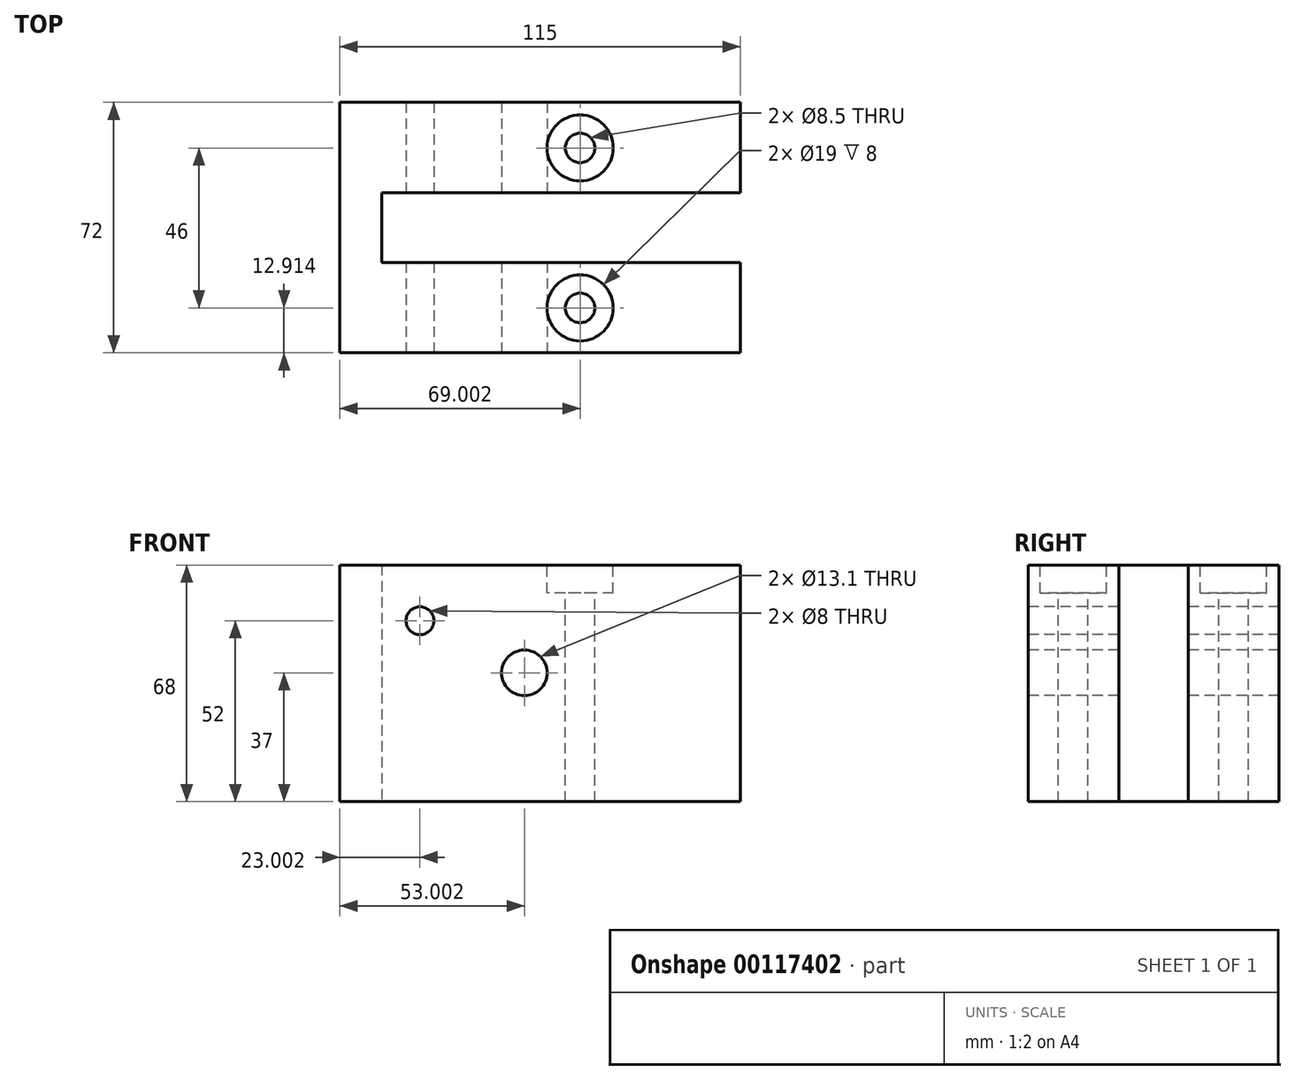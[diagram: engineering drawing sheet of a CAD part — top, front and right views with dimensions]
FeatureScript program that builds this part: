
annotation { "Feature Type Name" : "Feature", "Feature Type Description" : "" }
export const myFeature = defineFeature(function(context is Context, id is Id, definition is map)
    precondition{}
    {
        {
            var Q0;
            Q0=qCreatedBy(makeId("Top.planeOp"),FACE);
            var sketch = newSketch(context, id + "F0", { "sketchPlane" : qUnion([Q0])});
            skLineSegment(sketch, "E0.bottom", {"start": v(66.85, 38.03) * mm, "end": v(-48.15, 38.03) * mm});
            skLineSegment(sketch, "E0.top", {"start": v(66.85, -33.97) * mm, "end": v(-48.15, -33.97) * mm});
            skLineSegment(sketch, "E0.right", {"start": v(-48.15, 38.03) * mm, "end": v(-48.15, -33.97) * mm});
            skLineSegment(sketch, "E1.bottom", {"start": v(66.85, 12.03) * mm, "end": v(-36.15, 12.03) * mm});
            skLineSegment(sketch, "E1.top", {"start": v(66.85, -7.97) * mm, "end": v(-36.15, -7.97) * mm});
            skLineSegment(sketch, "E1.right", {"start": v(-36.15, 12.03) * mm, "end": v(-36.15, -7.97) * mm});
            skLineSegment(sketch, "E2", {"start": v(66.85, -33.97) * mm, "end": v(66.85, 38.03) * mm});
            skSolve(sketch);
        }
        {
            var Q0;
            {var subQ4=sQuery(id+"F0.wireOp",EDGE,"E0.bottom");Q0=makeQuery(id+"F0.imprint","IMPRINT",FACE,{"disambiguationData":[TD([[makeQuery(id+"F0.imprint","IMPRINT",EDGE,{"derivedFrom":subQ4}),1.0]])]});}
            extrude(context, id + "F1", {"entities" : qUnion([Q0]), "depth" : 68 * mm});
        }
        {
            var Q0;
            Q0=makeQuery(id+"F1.opExtrude","CAP_FACE",FACE,{"disambiguationData":[OSD([sQuery(id+"F0.wireOp",EDGE,"E0.bottom"),sQuery(id+"F0.wireOp",EDGE,"E0.top"),sQuery(id+"F0.wireOp",EDGE,"E0.left"),sQuery(id+"F0.wireOp",EDGE,"E0.right"),sQuery(id+"F0.wireOp",EDGE,"E1.bottom"),sQuery(id+"F0.wireOp",EDGE,"E1.top"),sQuery(id+"F0.wireOp",EDGE,"E1.right")])],"isStart":false});
            var sketch = newSketch(context, id + "F2", { "sketchPlane" : qUnion([Q0])});
            skCircle(sketch, "E3", {"center": v(20.85, 24.94) * mm, "radius": 9.5 * mm});
            skCircle(sketch, "E4", {"center": v(20.85, -21.06) * mm, "radius": 9.5 * mm});
            skSolve(sketch);
        }
        {
            var Q0;
            Q0=sQuery(id+"F2.wireOp",VERTEX,"E3.center");
            var Q1;
            Q1=sQuery(id+"F2.wireOp",VERTEX,"E4.center");
            var Q2;
            Q2=makeQuery(id+"F1.opExtrude","SWEPT_BODY",BODY,{"disambiguationData":[OSD([sQuery(id+"F0.wireOp",EDGE,"E0.bottom"),sQuery(id+"F0.wireOp",EDGE,"E0.top"),sQuery(id+"F0.wireOp",EDGE,"E0.left"),sQuery(id+"F0.wireOp",EDGE,"E0.right"),sQuery(id+"F0.wireOp",EDGE,"E1.bottom"),sQuery(id+"F0.wireOp",EDGE,"E1.top"),sQuery(id+"F0.wireOp",EDGE,"E1.right")])]});
            hole(context, id + "F3", {"style" : HoleStyle.C_BORE, "endStyle" : HoleEndStyle.THROUGH, "holeDiameter" : 8.5 * mm, "cBoreDiameter" : 19 * mm, "cBoreDepth" : 8 * mm, "locations" : qUnion([Q0, Q1]), "scope" : qUnion([Q2]), "isTappedThrough" : true});
        }
        {
            var Q0;
            Q0=makeQuery(id+"F1.opExtrude","SWEPT_FACE",FACE,{"disambiguationData":[OSD([sQuery(id+"F0.wireOp",EDGE,"E0.top")])]});
            var sketch = newSketch(context, id + "F4", { "sketchPlane" : qUnion([Q0])});
            skCircle(sketch, "E5", {"center": v(4.85, 37) * mm, "radius": 6.55 * mm});
            skCircle(sketch, "E6", {"center": v(-25.15, 52) * mm, "radius": 4 * mm});
            skSolve(sketch);
        }
        {
            var Q0;
            Q0=sQuery(id+"F4.wireOp",VERTEX,"E5.center");
            var Q1;
            Q1=makeQuery(id+"F1.opExtrude","SWEPT_BODY",BODY,{"disambiguationData":[OSD([sQuery(id+"F0.wireOp",EDGE,"E0.bottom"),sQuery(id+"F0.wireOp",EDGE,"E0.top"),sQuery(id+"F0.wireOp",EDGE,"E0.left"),sQuery(id+"F0.wireOp",EDGE,"E0.right"),sQuery(id+"F0.wireOp",EDGE,"E1.bottom"),sQuery(id+"F0.wireOp",EDGE,"E1.top"),sQuery(id+"F0.wireOp",EDGE,"E1.right")])]});
            hole(context, id + "F5", {"style" : HoleStyle.SIMPLE, "endStyle" : HoleEndStyle.THROUGH, "holeDiameter" : 13.1 * mm, "locations" : qUnion([Q0]), "scope" : qUnion([Q1]), "isTappedThrough" : true});
        }
        {
            var Q0;
            Q0=makeQuery(id+"F1.opExtrude","SWEPT_FACE",FACE,{"disambiguationData":[OSD([sQuery(id+"F0.wireOp",EDGE,"E0.top")])]});
            var sketch = newSketch(context, id + "F6", { "sketchPlane" : qUnion([Q0])});
            skCircle(sketch, "E7", {"center": v(-25.15, 52) * mm, "radius": 4 * mm});
            skSolve(sketch);
        }
        {
            var Q0;
            Q0=sQuery(id+"F6.wireOp",VERTEX,"E7.center");
            var Q1;
            Q1=makeQuery(id+"F1.opExtrude","SWEPT_BODY",BODY,{"disambiguationData":[OSD([sQuery(id+"F0.wireOp",EDGE,"E0.bottom"),sQuery(id+"F0.wireOp",EDGE,"E0.top"),sQuery(id+"F0.wireOp",EDGE,"E0.left"),sQuery(id+"F0.wireOp",EDGE,"E0.right"),sQuery(id+"F0.wireOp",EDGE,"E1.bottom"),sQuery(id+"F0.wireOp",EDGE,"E1.top"),sQuery(id+"F0.wireOp",EDGE,"E1.right")])]});
            hole(context, id + "F7", {"style" : HoleStyle.SIMPLE, "endStyle" : HoleEndStyle.THROUGH, "holeDiameter" : 8 * mm, "locations" : qUnion([Q0]), "scope" : qUnion([Q1]), "isTappedThrough" : true});
        }
    });
